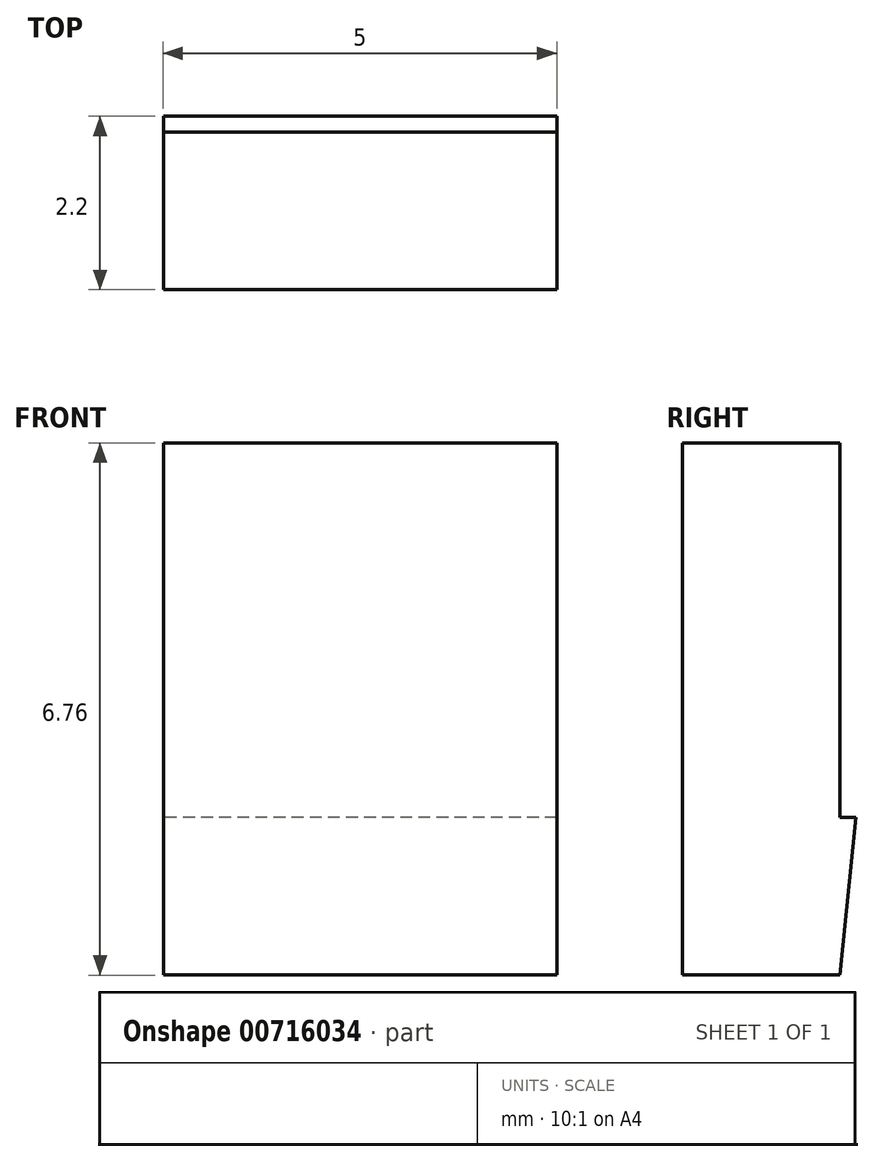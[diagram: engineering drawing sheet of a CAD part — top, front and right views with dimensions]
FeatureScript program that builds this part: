
annotation { "Feature Type Name" : "Feature", "Feature Type Description" : "" }
export const myFeature = defineFeature(function(context is Context, id is Id, definition is map)
    precondition{}
    {
        {
            var Q0;
            Q0=qCreatedBy(makeId("Front.planeOp"),FACE);
            var sketch = newSketch(context, id + "F0", { "sketchPlane" : qUnion([Q0])});
            skLineSegment(sketch, "E0.bottom", {"start": v(2.6, 0.64) * mm, "end": v(7.6, 0.64) * mm});
            skLineSegment(sketch, "E0.top", {"start": v(2.6, 7.4) * mm, "end": v(7.6, 7.4) * mm});
            skLineSegment(sketch, "E0.left", {"start": v(2.6, 0.64) * mm, "end": v(2.6, 7.4) * mm});
            skLineSegment(sketch, "E0.right", {"start": v(7.6, 0.64) * mm, "end": v(7.6, 7.4) * mm});
            skSolve(sketch);
        }
        {
            var Q0;
            Q0=qSketchRegion(id+"F0",true);
            extrude(context, id + "F1", {"entities" : qUnion([Q0]), "depth" : 2 * mm});
        }
        {
            var Q0;
            Q0=makeQuery(id+"F1.opExtrude","SWEPT_FACE",FACE,{"disambiguationData":[OSD([sQuery(id+"F0.wireOp",EDGE,"E0.left")])]});
            var sketch = newSketch(context, id + "F2", { "sketchPlane" : qUnion([Q0])});
            skLineSegment(sketch, "E1", {"start": v(0, 0.64) * mm, "end": v(0, 2.64) * mm});
            skLineSegment(sketch, "E2", {"start": v(0, 2.64) * mm, "end": v(-0.2, 2.64) * mm});
            skLineSegment(sketch, "E3", {"start": v(-0.2, 2.64) * mm, "end": v(0, 0.64) * mm});
            skSolve(sketch);
        }
        {
            var Q0;
            Q0=qSketchRegion(id+"F2",true);
            extrude(context, id + "F3", {"entities" : qUnion([Q0]), "operationType" : NewBodyOperationType.ADD, "oppositeDirection" : true, "depth" : 5 * mm});
        }
    });
